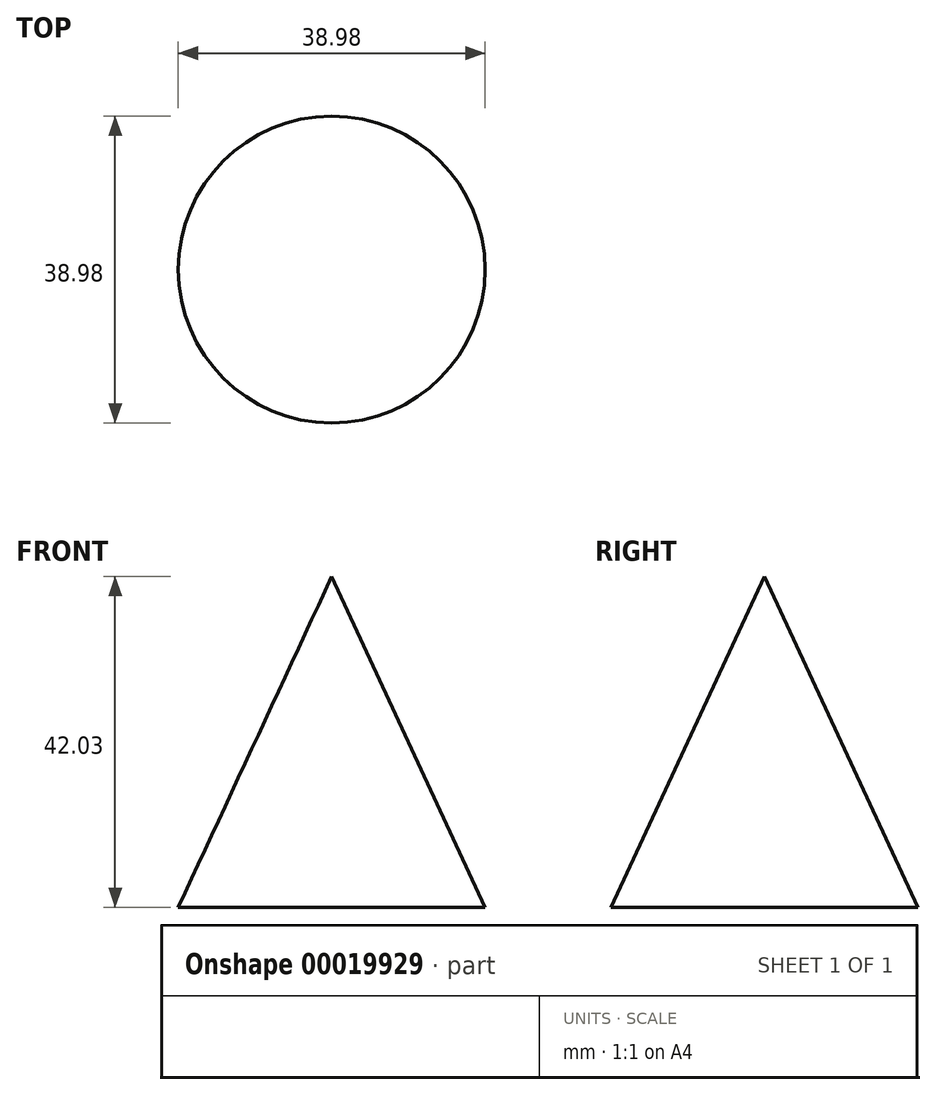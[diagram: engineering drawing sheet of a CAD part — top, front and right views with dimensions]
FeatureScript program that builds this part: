
annotation { "Feature Type Name" : "Feature", "Feature Type Description" : "" }
export const myFeature = defineFeature(function(context is Context, id is Id, definition is map)
    precondition{}
    {
        {
            var Q0;
            Q0=qCreatedBy(makeId("Front.planeOp"),FACE);
            var sketch = newSketch(context, id + "F0", { "sketchPlane" : qUnion([Q0])});
            skLineSegment(sketch, "E0", {"start": v(0, 0) * mm, "end": v(0, 42.03) * mm});
            skLineSegment(sketch, "E1", {"start": v(0, 42.03) * mm, "end": v(19.49, 0) * mm});
            skLineSegment(sketch, "E2", {"start": v(19.49, 0) * mm, "end": v(0, 0) * mm});
            skSolve(sketch);
        }
        {
            var Q0;
            Q0=makeQuery(id+"F0.imprint","IMPRINT",FACE,{"disambiguationData":[TD([[makeQuery(id+"F0.imprint","IMPRINT",EDGE,{"derivedFrom":sQuery(id+"F0.wireOp",EDGE,"E0")}),-1.0]])]});
            var Q1;
            Q1=sQuery(id+"F0.wireOp",EDGE,"E0");
            revolve(context, id + "F1", {"entities" : qUnion([Q0]), "axis" : qUnion([Q1]), "revolveType" : RevolveType.FULL});
        }
    });
